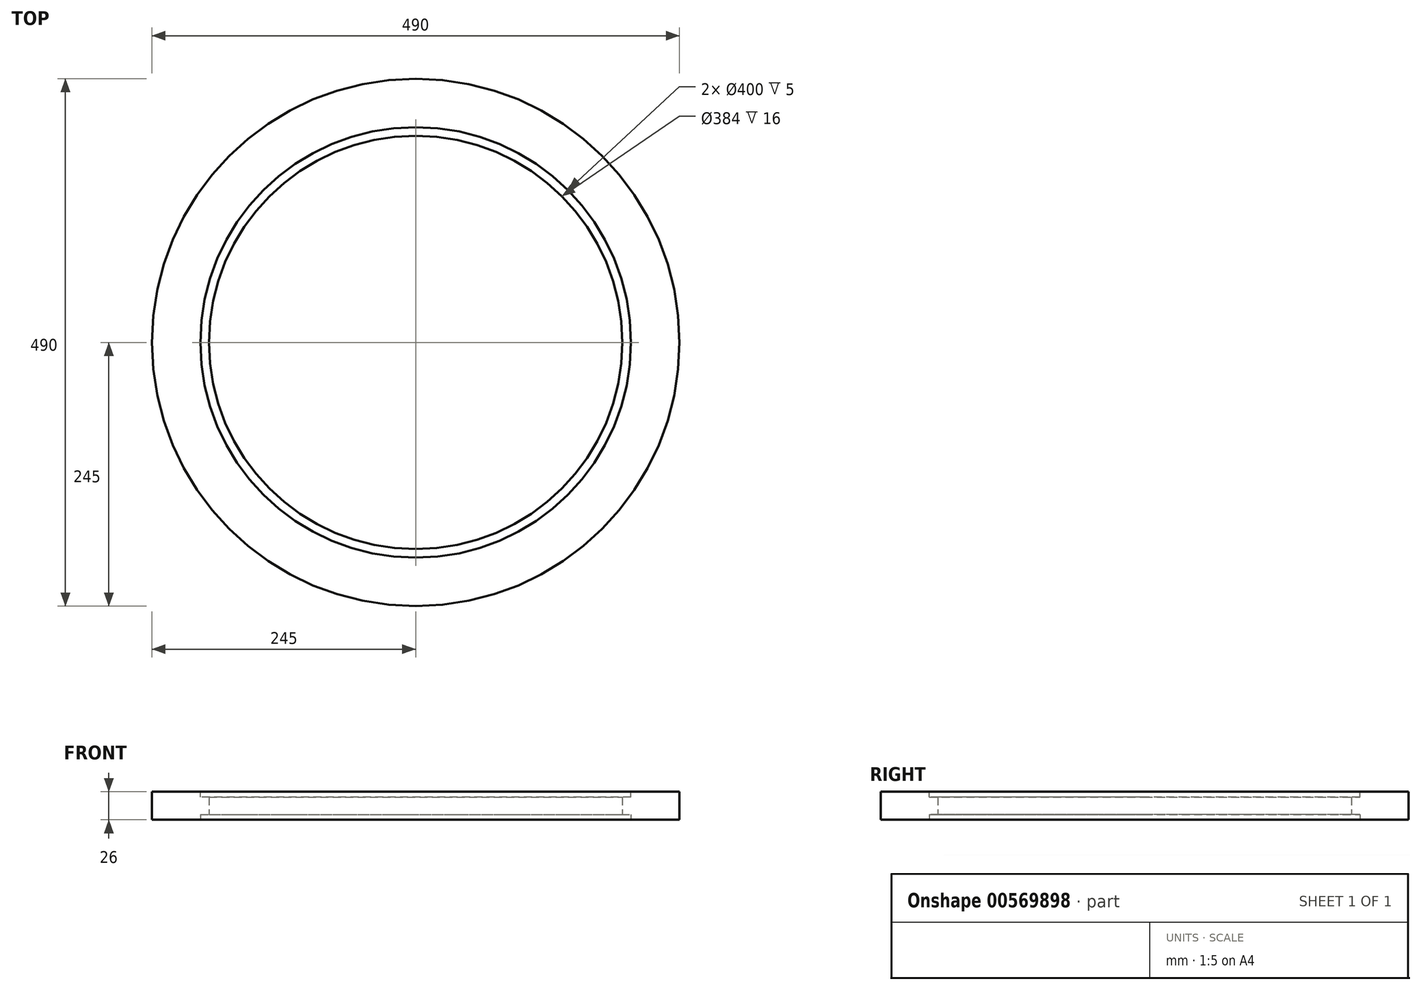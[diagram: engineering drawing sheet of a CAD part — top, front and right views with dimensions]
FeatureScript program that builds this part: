
annotation { "Feature Type Name" : "Feature", "Feature Type Description" : "" }
export const myFeature = defineFeature(function(context is Context, id is Id, definition is map)
    precondition{}
    {
        {
            var Q0;
            Q0=qCreatedBy(makeId("Top.planeOp"),FACE);
            var sketch = newSketch(context, id + "F0", { "sketchPlane" : qUnion([Q0])});
            skCircle(sketch, "E0", {"center": v(0, 0) * mm, "radius": 245 * mm});
            skCircle(sketch, "E1", {"center": v(0, 0) * mm, "radius": 192 * mm});
            skSolve(sketch);
        }
        {
            var Q0;
            Q0=qSketchRegion(id+"F0",true);
            extrude(context, id + "F1", {"entities" : qUnion([Q0]), "depth" : 26 * mm, "offsetDistance" : 25 * mm});
        }
        {
            var Q0;
            Q0=makeQuery(id+"F1.opExtrude","CAP_FACE",FACE,{"disambiguationData":[OSD([sQuery(id+"F0.wireOp",EDGE,"E0"),sQuery(id+"F0.wireOp",EDGE,"E1")])],"isStart":false});
            var sketch = newSketch(context, id + "F2", { "sketchPlane" : qUnion([Q0])});
            skCircle(sketch, "E2", {"center": v(0, 0) * mm, "radius": 200 * mm});
            skSolve(sketch);
        }
        {
            var Q0;
            Q0=qSketchRegion(id+"F2",true);
            extrude(context, id + "F3", {"entities" : qUnion([Q0]), "operationType" : NewBodyOperationType.REMOVE, "oppositeDirection" : true, "depth" : 5 * mm, "offsetDistance" : 25 * mm});
        }
        {
            var Q0;
            Q0=makeQuery(id+"F1.opExtrude","CAP_FACE",FACE,{"disambiguationData":[OSD([sQuery(id+"F0.wireOp",EDGE,"E0"),sQuery(id+"F0.wireOp",EDGE,"E1")])],"isStart":true});
            var sketch = newSketch(context, id + "F4", { "sketchPlane" : qUnion([Q0])});
            skCircle(sketch, "E3", {"center": v(0, 0) * mm, "radius": 200 * mm});
            skSolve(sketch);
        }
        {
            var Q0;
            Q0=qSketchRegion(id+"F4",true);
            extrude(context, id + "F5", {"entities" : qUnion([Q0]), "operationType" : NewBodyOperationType.REMOVE, "oppositeDirection" : true, "depth" : 5 * mm, "offsetDistance" : 25 * mm});
        }
    });
